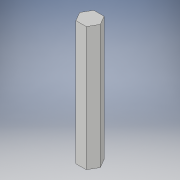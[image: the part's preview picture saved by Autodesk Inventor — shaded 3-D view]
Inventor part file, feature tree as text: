
AUTODESK INVENTOR PART (.ipt)
format: ipt  version: 2018 (Build 220112000, 112)  size: 94,720 bytes
history: native  units: in
note: dims shown in document units (in); Inventor stores cm internally (conversion verified against a paired STEP export)
features: extrude x1, sketch x1
ambient origin geometry x8: Origin, YZ Plane, XZ Plane, XY Plane, X Axis, Y Axis, Z Axis, Center Point
bodies: Solid1 (feature_tree)
feature tree (2):
  extrude  "Extrusion1"  Depth=3.5in TaperAngle=0.0deg
  sketch  "Sketch1"  dims[d0=0.582in d1=3.5in d2=0.0in]
